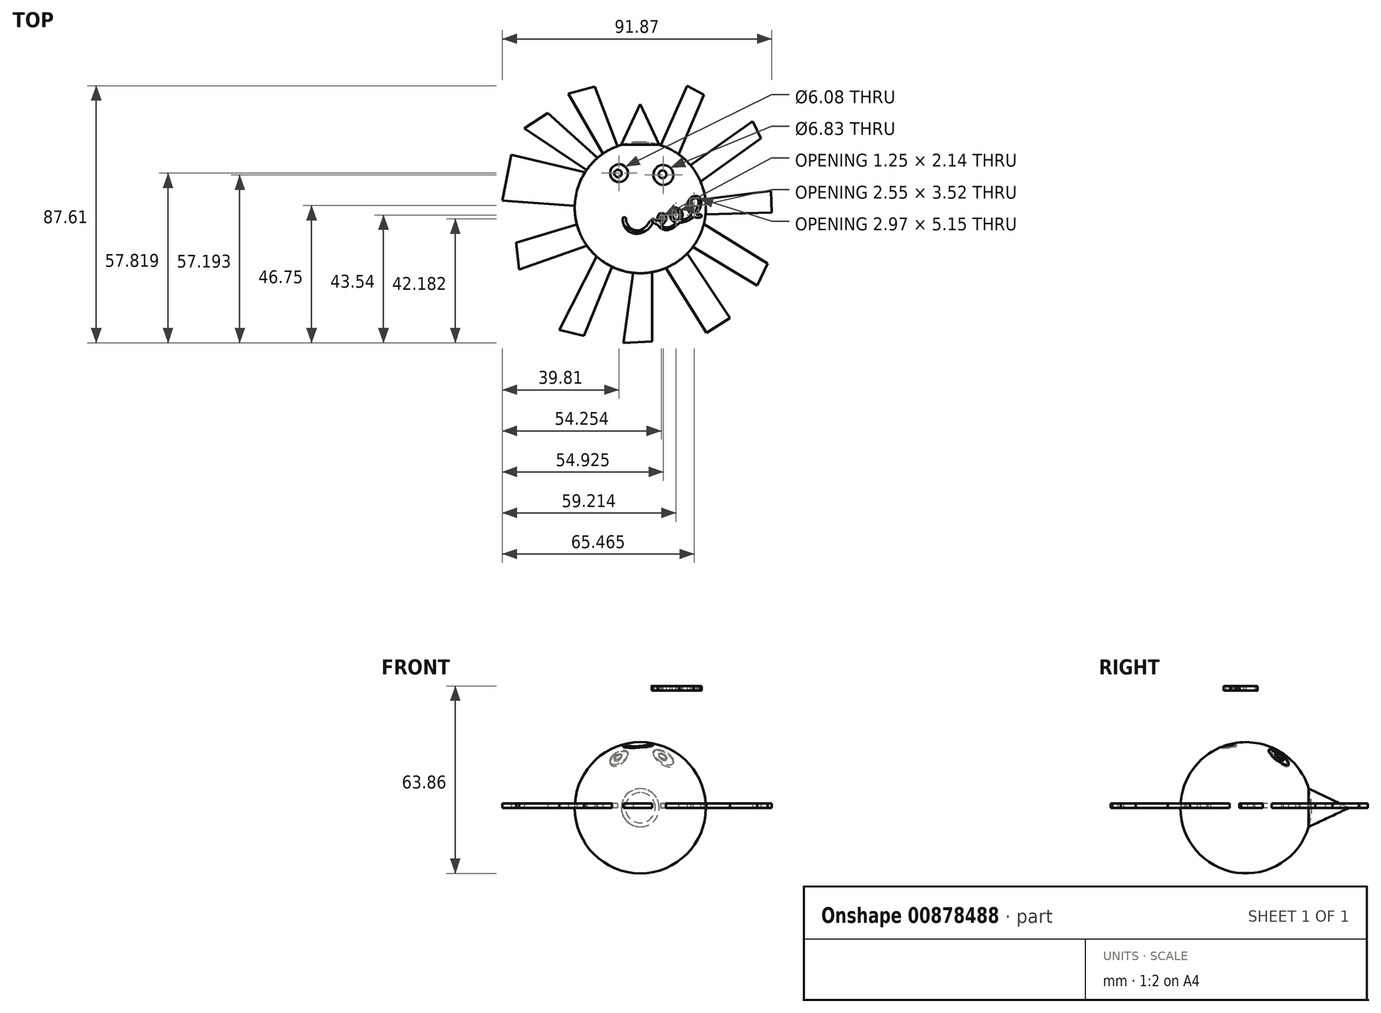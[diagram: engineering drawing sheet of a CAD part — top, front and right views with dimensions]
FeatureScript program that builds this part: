
annotation { "Feature Type Name" : "Feature", "Feature Type Description" : "" }
export const myFeature = defineFeature(function(context is Context, id is Id, definition is map)
    precondition{}
    {
        {
            var Q0;
            Q0=qCreatedBy(makeId("Top.planeOp"),FACE);
            var sketch = newSketch(context, id + "F0", { "sketchPlane" : qUnion([Q0])});
            skLineSegment(sketch, "E0.bottom", {"start": v(-19.28, 52.94) * mm, "end": v(90.72, 52.94) * mm});
            skLineSegment(sketch, "E0.top", {"start": v(-19.28, -37.16) * mm, "end": v(90.72, -37.16) * mm});
            skLineSegment(sketch, "E0.left", {"start": v(-19.28, 52.94) * mm, "end": v(-19.28, -37.16) * mm});
            skLineSegment(sketch, "E0.right", {"start": v(90.72, 52.94) * mm, "end": v(90.72, -37.16) * mm});
            skCircle(sketch, "E1", {"center": v(28.82, 9.49) * mm, "radius": 22.36 * mm});
            skCircle(sketch, "E2", {"center": v(21.2, 21.15) * mm, "radius": 1.26 * mm});
            skCircle(sketch, "E3", {"center": v(21.55, 21.24) * mm, "radius": 3.04 * mm});
            skCircle(sketch, "E4", {"center": v(36.4, 20.84) * mm, "radius": 1.33 * mm});
            skCircle(sketch, "E5", {"center": v(36.66, 20.61) * mm, "radius": 3.41 * mm});
            skLineSegment(sketch, "E6", {"start": v(28.82, 9.49) * mm, "end": v(28.82, 46.5) * mm});
            skLineSegment(sketch, "E7", {"start": v(28.82, 44.72) * mm, "end": v(22.34, 30.89) * mm});
            skLineSegment(sketch, "E8", {"start": v(28.82, 9.49) * mm, "end": v(28.82, -19.3) * mm});
            skLineSegment(sketch, "E9", {"start": v(22.34, 30.89) * mm, "end": v(28.82, 30.89) * mm});
            skLineSegment(sketch, "E10", {"start": v(21.06, 30.46) * mm, "end": v(13.28, 50.77) * mm});
            skLineSegment(sketch, "E11", {"start": v(13.28, 50.77) * mm, "end": v(4.25, 48.33) * mm});
            skLineSegment(sketch, "E12", {"start": v(4.25, 48.33) * mm, "end": v(16.12, 27.9) * mm});
            skLineSegment(sketch, "E13", {"start": v(14.23, 26.43) * mm, "end": v(-2.77, 41.68) * mm});
            skLineSegment(sketch, "E14", {"start": v(-2.77, 41.68) * mm, "end": v(-10.67, 36.54) * mm});
            skLineSegment(sketch, "E15", {"start": v(-10.67, 36.54) * mm, "end": v(10.46, 22.24) * mm});
            skLineSegment(sketch, "E16", {"start": v(9.97, 21.5) * mm, "end": v(-15.12, 27.5) * mm});
            skLineSegment(sketch, "E17", {"start": v(-15.12, 27.5) * mm, "end": v(-18.26, 11.9) * mm});
            skLineSegment(sketch, "E18", {"start": v(-18.26, 11.9) * mm, "end": v(6.47, 10.07) * mm});
            skLineSegment(sketch, "E19", {"start": v(7.2, 3.76) * mm, "end": v(-13.56, -2.53) * mm});
            skLineSegment(sketch, "E20", {"start": v(-13.56, -2.53) * mm, "end": v(-12.55, -11.56) * mm});
            skLineSegment(sketch, "E21", {"start": v(-12.55, -11.56) * mm, "end": v(10.6, -3.47) * mm});
            skLineSegment(sketch, "E22", {"start": v(13.94, -7.2) * mm, "end": v(1.18, -32.25) * mm});
            skLineSegment(sketch, "E23", {"start": v(1.18, -32.25) * mm, "end": v(9.65, -34.2) * mm});
            skLineSegment(sketch, "E24", {"start": v(9.65, -34.2) * mm, "end": v(19.15, -10.67) * mm});
            skLineSegment(sketch, "E25", {"start": v(26.4, -12.74) * mm, "end": v(23, -36.58) * mm});
            skLineSegment(sketch, "E26", {"start": v(23, -36.58) * mm, "end": v(32.91, -36.08) * mm});
            skLineSegment(sketch, "E27", {"start": v(32.91, -36.08) * mm, "end": v(32.91, -12.5) * mm});
            skLineSegment(sketch, "E28", {"start": v(37.5, -11.12) * mm, "end": v(51.35, -33.2) * mm});
            skLineSegment(sketch, "E29", {"start": v(51.35, -33.2) * mm, "end": v(59.44, -28.12) * mm});
            skLineSegment(sketch, "E30", {"start": v(59.44, -28.12) * mm, "end": v(44.78, -6.17) * mm});
            skLineSegment(sketch, "E31", {"start": v(46.7, -3.93) * mm, "end": v(68.65, -17.14) * mm});
            skLineSegment(sketch, "E32", {"start": v(68.65, -17.14) * mm, "end": v(72.17, -9.62) * mm});
            skLineSegment(sketch, "E33", {"start": v(72.17, -9.62) * mm, "end": v(50.47, 3.88) * mm});
            skLineSegment(sketch, "E34", {"start": v(51.06, 7.19) * mm, "end": v(73.6, 7.82) * mm});
            skLineSegment(sketch, "E35", {"start": v(73.6, 7.82) * mm, "end": v(73.4, 15.16) * mm});
            skLineSegment(sketch, "E36", {"start": v(73.4, 15.16) * mm, "end": v(51, 12.37) * mm});
            skLineSegment(sketch, "E37", {"start": v(49.37, 18.31) * mm, "end": v(69.9, 33.09) * mm});
            skLineSegment(sketch, "E38", {"start": v(69.9, 33.09) * mm, "end": v(67.15, 38.98) * mm});
            skLineSegment(sketch, "E39", {"start": v(67.15, 38.98) * mm, "end": v(45.86, 23.97) * mm});
            skLineSegment(sketch, "E40", {"start": v(35.8, 30.73) * mm, "end": v(44.82, 51.03) * mm});
            skLineSegment(sketch, "E41", {"start": v(44.82, 51.03) * mm, "end": v(50.47, 47.95) * mm});
            skLineSegment(sketch, "E42", {"start": v(50.47, 47.95) * mm, "end": v(41.92, 27.61) * mm});
            skCircle(sketch, "E43", {"center": v(28.82, 9.49) * mm, "radius": 22 * mm});
            skSolve(sketch);
        }
        {
            var Q0;
            Q0=makeQuery(id+"F0.imprint","IMPRINT",FACE,{"disambiguationData":[TD([[makeQuery(id+"F0.imprint","IMPRINT",EDGE,{"derivedFrom":sQuery(id+"F0.wireOp",EDGE,"E3")}),-1.0]])]});
            var Q1;
            Q1=makeQuery(id+"F0.imprint","IMPRINT",FACE,{"disambiguationData":[TD([[makeQuery(id+"F0.imprint","IMPRINT",EDGE,{"derivedFrom":sQuery(id+"F0.wireOp",EDGE,"E2")}),1.0]])]});
            var Q2;
            Q2=makeQuery(id+"F0.imprint","IMPRINT",FACE,{"disambiguationData":[TD([[makeQuery(id+"F0.imprint","IMPRINT",EDGE,{"derivedFrom":sQuery(id+"F0.wireOp",EDGE,"E2")}),-1.0]])]});
            var Q3;
            {var subQ0=sQuery(id+"F0.wireOp",EDGE,"E1");var subQ15=makeQuery(id+"F0.imprint","INTERSECT",VERTEX,{"derivedFrom":[subQ0,sQuery(id+"F0.wireOp",EDGE,"E10")]});Q3=makeQuery(id+"F0.imprint","IMPRINT",FACE,{"disambiguationData":[TD([[makeQuery(id+"F0.imprint","IMPRINT",EDGE,{"disambiguationData":[TD([[subQ15,-1.0]])],"derivedFrom":subQ0}),1.0]])]});}
            var Q4;
            Q4=sQuery(id+"F0.wireOp",EDGE,"E6");
            revolve(context, id + "F1", {"surfaceOperationType" : NewSurfaceOperationType.NEW, "entities" : qUnion([Q0, Q1, Q2, Q3]), "axis" : qUnion([Q4]), "revolveType" : RevolveType.FULL});
        }
        {
            var Q0;
            {var subQ0=sQuery(id+"F0.wireOp",EDGE,"E7");Q0=makeQuery(id+"F0.imprint","IMPRINT",FACE,{"disambiguationData":[TD([[makeQuery(id+"F0.imprint","IMPRINT",EDGE,{"derivedFrom":subQ0}),1.0]])]});}
            var Q1;
            {var subQ0=sQuery(id+"F0.wireOp",EDGE,"E9");Q1=makeQuery(id+"F0.imprint","IMPRINT",FACE,{"disambiguationData":[TD([[makeQuery(id+"F0.imprint","IMPRINT",EDGE,{"derivedFrom":subQ0}),1.0]])]});}
            var Q2;
            Q2=sQuery(id+"F0.wireOp",EDGE,"E6");
            revolve(context, id + "F2", {"surfaceOperationType" : NewSurfaceOperationType.NEW, "entities" : qUnion([Q0, Q1]), "axis" : qUnion([Q2]), "revolveType" : RevolveType.FULL});
        }
        {
            var Q0;
            {var subQ0=sQuery(id+"F0.wireOp",EDGE,"E10");Q0=makeQuery(id+"F0.imprint","IMPRINT",FACE,{"disambiguationData":[TD([[makeQuery(id+"F0.imprint","IMPRINT",EDGE,{"derivedFrom":subQ0}),1.0]])]});}
            var Q1;
            {var subQ0=sQuery(id+"F0.wireOp",EDGE,"E40");Q1=makeQuery(id+"F0.imprint","IMPRINT",FACE,{"disambiguationData":[TD([[makeQuery(id+"F0.imprint","IMPRINT",EDGE,{"derivedFrom":subQ0}),-1.0]])]});}
            var Q2;
            {var subQ0=sQuery(id+"F0.wireOp",EDGE,"E37");Q2=makeQuery(id+"F0.imprint","IMPRINT",FACE,{"disambiguationData":[TD([[makeQuery(id+"F0.imprint","IMPRINT",EDGE,{"derivedFrom":subQ0}),1.0]])]});}
            var Q3;
            {var subQ0=sQuery(id+"F0.wireOp",EDGE,"E34");Q3=makeQuery(id+"F0.imprint","IMPRINT",FACE,{"disambiguationData":[TD([[makeQuery(id+"F0.imprint","IMPRINT",EDGE,{"derivedFrom":subQ0}),1.0]])]});}
            var Q4;
            {var subQ0=sQuery(id+"F0.wireOp",EDGE,"E31");Q4=makeQuery(id+"F0.imprint","IMPRINT",FACE,{"disambiguationData":[TD([[makeQuery(id+"F0.imprint","IMPRINT",EDGE,{"derivedFrom":subQ0}),1.0]])]});}
            var Q5;
            {var subQ0=sQuery(id+"F0.wireOp",EDGE,"E28");Q5=makeQuery(id+"F0.imprint","IMPRINT",FACE,{"disambiguationData":[TD([[makeQuery(id+"F0.imprint","IMPRINT",EDGE,{"derivedFrom":subQ0}),1.0]])]});}
            var Q6;
            {var subQ3=sQuery(id+"F0.wireOp",EDGE,"E25");Q6=makeQuery(id+"F0.imprint","IMPRINT",FACE,{"disambiguationData":[TD([[makeQuery(id+"F0.imprint","IMPRINT",EDGE,{"derivedFrom":subQ3}),1.0]])]});}
            var Q7;
            {var subQ0=sQuery(id+"F0.wireOp",EDGE,"E22");Q7=makeQuery(id+"F0.imprint","IMPRINT",FACE,{"disambiguationData":[TD([[makeQuery(id+"F0.imprint","IMPRINT",EDGE,{"derivedFrom":subQ0}),1.0]])]});}
            var Q8;
            {var subQ0=sQuery(id+"F0.wireOp",EDGE,"E19");Q8=makeQuery(id+"F0.imprint","IMPRINT",FACE,{"disambiguationData":[TD([[makeQuery(id+"F0.imprint","IMPRINT",EDGE,{"derivedFrom":subQ0}),1.0]])]});}
            var Q9;
            {var subQ0=sQuery(id+"F0.wireOp",EDGE,"E16");Q9=makeQuery(id+"F0.imprint","IMPRINT",FACE,{"disambiguationData":[TD([[makeQuery(id+"F0.imprint","IMPRINT",EDGE,{"derivedFrom":subQ0}),1.0]])]});}
            var Q10;
            {var subQ0=sQuery(id+"F0.wireOp",EDGE,"E13");Q10=makeQuery(id+"F0.imprint","IMPRINT",FACE,{"disambiguationData":[TD([[makeQuery(id+"F0.imprint","IMPRINT",EDGE,{"derivedFrom":subQ0}),1.0]])]});}
            extrude(context, id + "F3", {"entities" : qUnion([Q0, Q1, Q2, Q3, Q4, Q5, Q6, Q7, Q8, Q9, Q10]), "depth" : 1.5 * mm, "offsetDistance" : 25 * mm});
        }
        {
            var Q0;
            Q0=qCreatedBy(makeId("Top.planeOp"),FACE);
            var sketch = newSketch(context, id + "F4", { "sketchPlane" : qUnion([Q0])});
            skCircle(sketch, "E44", {"center": v(23.33, 5.63) * mm, "radius": 0.53 * mm});
            skCircle(sketch, "E45", {"center": v(33.22, 5.16) * mm, "radius": 0.54 * mm});
            skCircle(sketch, "E46", {"center": v(49.22, 6.66) * mm, "radius": 0.5 * mm});
            skFitSpline(sketch, "E47", {"points": [v(32.91, 4.7) * mm, v(36.32, 7.58) * mm], "startDerivative": vector(11.73, -10.55) * mm, "endDerivative": vector(-9.17, 1.96) * mm});
            skFitSpline(sketch, "E48", {"points": [v(33.44, 5.65) * mm, v(36.21, 6.65) * mm], "startDerivative": vector(9.78, -8.8) * mm, "endDerivative": vector(-2.68, 0.78) * mm});
            skFitSpline(sketch, "E49", {"points": [v(35.4, 4.53) * mm, v(36.21, 6.65) * mm], "startDerivative": vector(-0.43, 2.5) * mm, "endDerivative": vector(2.13, -0.84) * mm});
            skFitSpline(sketch, "E50", {"points": [v(34.5, 4.86) * mm, v(36.32, 7.58) * mm], "startDerivative": vector(-0.22, 5.03) * mm, "endDerivative": vector(3.52, -0.5) * mm});
            skFitSpline(sketch, "E51", {"points": [v(35.72, 3.6) * mm, v(40.74, 8.72) * mm], "startDerivative": vector(11.64, -10.8) * mm, "endDerivative": vector(-12.34, 1.4) * mm});
            skFitSpline(sketch, "E52", {"points": [v(40.74, 8.72) * mm, v(41.61, 5.2) * mm], "startDerivative": vector(-5.62, 0.4) * mm, "endDerivative": vector(5.86, 0.34) * mm});
            skFitSpline(sketch, "E53", {"points": [v(34.7, 3.66) * mm, v(40.74, 9.5) * mm], "startDerivative": vector(10.96, -17.87) * mm, "endDerivative": vector(-20.66, 3.88) * mm});
            skFitSpline(sketch, "E54", {"points": [v(40.74, 9.5) * mm, v(41, 4.36) * mm], "startDerivative": vector(-7.71, 0.77) * mm, "endDerivative": vector(8.73, -2.24) * mm});
            skFitSpline(sketch, "E55", {"points": [v(48.27, 12.5) * mm, v(42.69, 5.25) * mm], "startDerivative": vector(5.15, -5.6) * mm, "endDerivative": vector(-10.93, -0.46) * mm});
            skFitSpline(sketch, "E56", {"points": [v(42.07, 4.32) * mm, v(48.57, 13.25) * mm], "startDerivative": vector(21, 1.8) * mm, "endDerivative": vector(-7.28, 3.14) * mm});
            skFitSpline(sketch, "E57", {"points": [v(46.96, 7.6) * mm, v(48.27, 12.5) * mm], "startDerivative": vector(-9.1, 7.81) * mm, "endDerivative": vector(3.47, -3.58) * mm});
            skFitSpline(sketch, "E58", {"points": [v(47.87, 7.17) * mm, v(49.13, 7.15) * mm], "startDerivative": vector(1.47, -0.5) * mm, "endDerivative": vector(1.57, 0.6) * mm});
            skFitSpline(sketch, "E59", {"points": [v(48.57, 13.25) * mm, v(46.33, 6.96) * mm], "startDerivative": vector(-8.62, 3.72) * mm, "endDerivative": vector(9.71, -8.54) * mm});
            skFitSpline(sketch, "E60", {"points": [v(47.12, 6.4) * mm, v(49.17, 6.16) * mm], "startDerivative": vector(1.7, -1) * mm, "endDerivative": vector(2.31, 0.72) * mm});
            skSolve(sketch);
        }
        {
            var Q0;
            {var subQ8=sQuery(id+"F4.wireOp",EDGE,"E49");Q0=makeQuery(id+"F4.imprint","IMPRINT",FACE,{"disambiguationData":[TD([[makeQuery(id+"F4.imprint","IMPRINT",EDGE,{"derivedFrom":subQ8}),1.0]])]});}
            var Q1;
            {var subQ0=sQuery(id+"F4.wireOp",EDGE,"E45");var subQ1=makeQuery(id+"F4.imprint","INTERSECT",VERTEX,{"derivedFrom":[subQ0,sQuery(id+"F4.wireOp",EDGE,"E47")]});Q1=makeQuery(id+"F4.imprint","IMPRINT",FACE,{"disambiguationData":[TD([[makeQuery(id+"F4.imprint","IMPRINT",EDGE,{"disambiguationData":[TD([[subQ1,1.0]])],"derivedFrom":subQ0}),1.0]])]});}
            var Q2;
            {var subQ0=sQuery(id+"F4.wireOp",EDGE,"E52");Q2=makeQuery(id+"F4.imprint","IMPRINT",FACE,{"disambiguationData":[TD([[makeQuery(id+"F4.imprint","IMPRINT",EDGE,{"derivedFrom":subQ0}),-1.0]])]});}
            var Q3;
            {var subQ4=sQuery(id+"F4.wireOp",EDGE,"E57");Q3=makeQuery(id+"F4.imprint","IMPRINT",FACE,{"disambiguationData":[TD([[makeQuery(id+"F4.imprint","IMPRINT",EDGE,{"derivedFrom":subQ4}),1.0]])]});}
            var Q4;
            {var subQ0=sQuery(id+"F4.wireOp",EDGE,"E60");Q4=makeQuery(id+"F4.imprint","IMPRINT",FACE,{"disambiguationData":[TD([[makeQuery(id+"F4.imprint","IMPRINT",EDGE,{"derivedFrom":subQ0}),1.0]])]});}
            var Q5;
            {var subQ0=sQuery(id+"F4.wireOp",EDGE,"E46");var subQ1=makeQuery(id+"F4.imprint","INTERSECT",VERTEX,{"derivedFrom":[subQ0,sQuery(id+"F4.wireOp",EDGE,"E60")]});Q5=makeQuery(id+"F4.imprint","IMPRINT",FACE,{"disambiguationData":[TD([[makeQuery(id+"F4.imprint","IMPRINT",EDGE,{"disambiguationData":[TD([[subQ1,1.0]])],"derivedFrom":subQ0}),1.0]])]});}
            extrude(context, id + "F5", {"entities" : qUnion([Q0, Q1, Q2, Q3, Q4, Q5]), "depth" : 41.5 * mm, "offsetDistance" : 25 * mm, "hasSecondDirection" : true, "secondDirectionOppositeDirection" : false, "secondDirectionDepth" : 40 * mm});
        }
        {
            var Q0;
            Q0=qCreatedBy(makeId("Top.planeOp"),FACE);
            var sketch = newSketch(context, id + "F6", { "sketchPlane" : qUnion([Q0])});
            skCircle(sketch, "E61", {"center": v(23.36, 5.61) * mm, "radius": 0.6 * mm});
            skCircle(sketch, "E62", {"center": v(32.64, 4.8) * mm, "radius": 0.6 * mm});
            skFitSpline(sketch, "E63", {"points": [v(23.96, 5.54) * mm, v(32.05, 4.92) * mm], "startDerivative": vector(-0.54, -7.83) * mm, "endDerivative": vector(10.82, 18.79) * mm});
            skFitSpline(sketch, "E64", {"points": [v(33.15, 4.49) * mm, v(22.75, 5.61) * mm], "startDerivative": vector(-6.2, -14.8) * mm, "endDerivative": vector(-1.66, 20.8) * mm});
            skLineSegment(sketch, "E65", {"start": v(32.05, 4.92) * mm, "end": v(33.15, 4.49) * mm});
            skLineSegment(sketch, "E66", {"start": v(23.96, 5.54) * mm, "end": v(22.75, 5.61) * mm});
            skSolve(sketch);
        }
        {
            var Q0;
            {var subQ0=sQuery(id+"F6.wireOp",EDGE,"E66");Q0=makeQuery(id+"F6.imprint","IMPRINT",FACE,{"disambiguationData":[TD([[makeQuery(id+"F6.imprint","IMPRINT",EDGE,{"derivedFrom":subQ0}),-1.0]])]});}
            var Q1;
            {var subQ0=sQuery(id+"F6.wireOp",EDGE,"E66");Q1=makeQuery(id+"F6.imprint","IMPRINT",FACE,{"disambiguationData":[TD([[makeQuery(id+"F6.imprint","IMPRINT",EDGE,{"derivedFrom":subQ0}),1.0]])]});}
            var Q2;
            {var subQ0=sQuery(id+"F6.wireOp",EDGE,"E63");Q2=makeQuery(id+"F6.imprint","IMPRINT",FACE,{"disambiguationData":[TD([[makeQuery(id+"F6.imprint","IMPRINT",EDGE,{"derivedFrom":subQ0}),-1.0]])]});}
            var Q3;
            {var subQ0=sQuery(id+"F6.wireOp",EDGE,"E65");Q3=makeQuery(id+"F6.imprint","IMPRINT",FACE,{"disambiguationData":[TD([[makeQuery(id+"F6.imprint","IMPRINT",EDGE,{"derivedFrom":subQ0}),-1.0]])]});}
            var Q4;
            {var subQ0=sQuery(id+"F6.wireOp",EDGE,"E65");Q4=makeQuery(id+"F6.imprint","IMPRINT",FACE,{"disambiguationData":[TD([[makeQuery(id+"F6.imprint","IMPRINT",EDGE,{"derivedFrom":subQ0}),1.0]])]});}
            extrude(context, id + "F7", {"entities" : qUnion([Q0, Q1, Q2, Q3, Q4]), "operationType" : NewBodyOperationType.REMOVE, "depth" : 31.5 * mm, "offsetDistance" : 25 * mm, "hasSecondDirection" : true, "secondDirectionOppositeDirection" : false, "secondDirectionDepth" : 20.43 * mm});
        }
        {
            var Q0;
            Q0=makeQuery(id+"F0.imprint","IMPRINT",FACE,{"disambiguationData":[TD([[makeQuery(id+"F0.imprint","IMPRINT",EDGE,{"derivedFrom":sQuery(id+"F0.wireOp",EDGE,"E4")}),-1.0]])]});
            var Q1;
            Q1=makeQuery(id+"F0.imprint","IMPRINT",FACE,{"disambiguationData":[TD([[makeQuery(id+"F0.imprint","IMPRINT",EDGE,{"derivedFrom":sQuery(id+"F0.wireOp",EDGE,"E2")}),-1.0]])]});
            extrude(context, id + "F8", {"entities" : qUnion([Q0, Q1]), "operationType" : NewBodyOperationType.REMOVE, "depth" : 27.4 * mm, "offsetDistance" : 25 * mm, "hasSecondDirection" : true, "secondDirectionOppositeDirection" : false, "secondDirectionDepth" : 13.2 * mm});
        }
        {
            var Q0;
            Q0=makeQuery(id+"F0.imprint","IMPRINT",FACE,{"disambiguationData":[TD([[makeQuery(id+"F0.imprint","IMPRINT",EDGE,{"derivedFrom":sQuery(id+"F0.wireOp",EDGE,"E3")}),-1.0]])]});
            var Q1;
            Q1=sQuery(id+"F0.wireOp",EDGE,"E6");
            revolve(context, id + "F9", {"operationType" : NewBodyOperationType.ADD, "surfaceOperationType" : NewSurfaceOperationType.NEW, "entities" : qUnion([Q0]), "axis" : qUnion([Q1]), "revolveType" : RevolveType.FULL});
        }
    });
